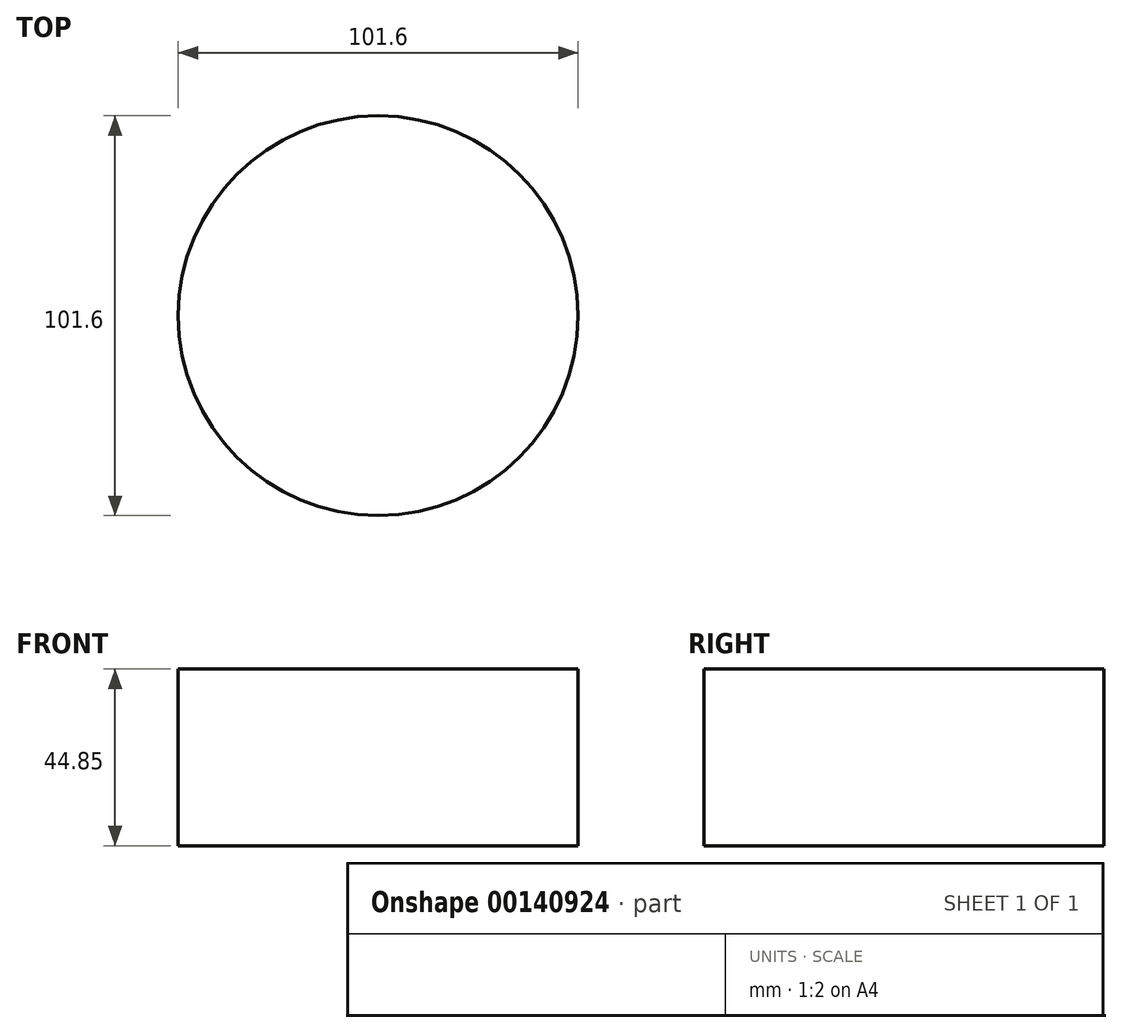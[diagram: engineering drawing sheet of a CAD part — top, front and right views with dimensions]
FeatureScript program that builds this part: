
annotation { "Feature Type Name" : "Feature", "Feature Type Description" : "" }
export const myFeature = defineFeature(function(context is Context, id is Id, definition is map)
    precondition{}
    {
        {
            var Q0;
            Q0=qCreatedBy(makeId("Top.planeOp"),FACE);
            var sketch = newSketch(context, id + "F0", { "sketchPlane" : qUnion([Q0])});
            skCircle(sketch, "E0", {"center": v(0, 0) * mm, "radius": 50.8 * mm});
            skSolve(sketch);
        }
        {
            var Q0;
            Q0 = qSketchRegion(id + "F0", true);
            extrude(context, id + "F1", {"entities" : qUnion([Q0]), "depth" : 44.85 * mm});
        }
    });
